# Revit family: Faucet-Lavatory-KOHLER-Purist-K-14402IN_1
name_source: partatom
category: Plumbing Fixtures
revit_build: Autodesk Revit 2017 (Build: 20160225_1515(x64)
units: mm (PartAtom-declared; Revit-internal decimal feet)

## family parameters
Cut with Voids When Loaded = No
Host = Face
OmniClass Number = 23.31.11.00
OmniClass Title = Faucets
Part Type = Normal
Room Calculation Point = No
Round Connector Dimension = Use Diameter
Shared = No

## types (4) — shared parameters
ADA Compliant = No
Assembly Code = D2010
CW Connection = Yes
Cold Water Inlet = Cold Water Inlet
Date Modified = 07/31/2020
Default Elevation = 36"
Flow Rate = 0 GPM
HW Connection = Yes
Handle Clearance = 3 1/4"
Hot Water Inlet = Hot Water Inlet
Length = 5 1/2"
Manufacturer = KOHLER Co.
Master Format 2014 = 22 41 39
Master Format 2014 Name = Residential Faucets, Supplies, and Trim
Material = Premium Metal Construction
Pressure = 0.00 psi
Product Name = Purist
Spout Reach = 5 1/2"
URL = https://www.kohler.co.in
Vent Connection = No
Waste Connection = No
Waste Water Outlet = Waste Water Outlet
WaterSense Certified = No
Width = 2 1/4"

## per-type parameters (varying)
| type | Description | Drain Included | Finish | Height | Model | Smile Design Handle | Straight Lever Handle | Type |
| 4, CP-Polished Chrome | Single-hole bathroom sink faucet with smile design handle | Yes | Kohler-Metal-CP-Polished_Chrome | 8" | K-14402IN-4-CP | Yes | No | 1 |
| 4A, CP-Polished Chrome | Single-handle bathroom sink faucet with straight lever handle | Yes | Kohler-Metal-CP-Polished_Chrome | 7 3/4" | K-14402IN-4A-CP | No | Yes | 2 |
| 4AND, BL-Matte Black | Single-handle bathroom sink faucet with straight lever handle | No | Kohler-Metal-BL-Matte_Black | 7 3/4" | K-14402IN-4AND-BL | No | Yes | 4 |
| 4AND, CP-Polished Chrome | Single-handle bathroom sink faucet with straight lever handle | No | Kohler-Metal-CP-Polished_Chrome | 7 3/4" | K-14402IN-4AND-CP | No | Yes | 3 |

## geometry (parser evidence)
native form markers: Sweep x5
no freeform markers — native parametric forms only
